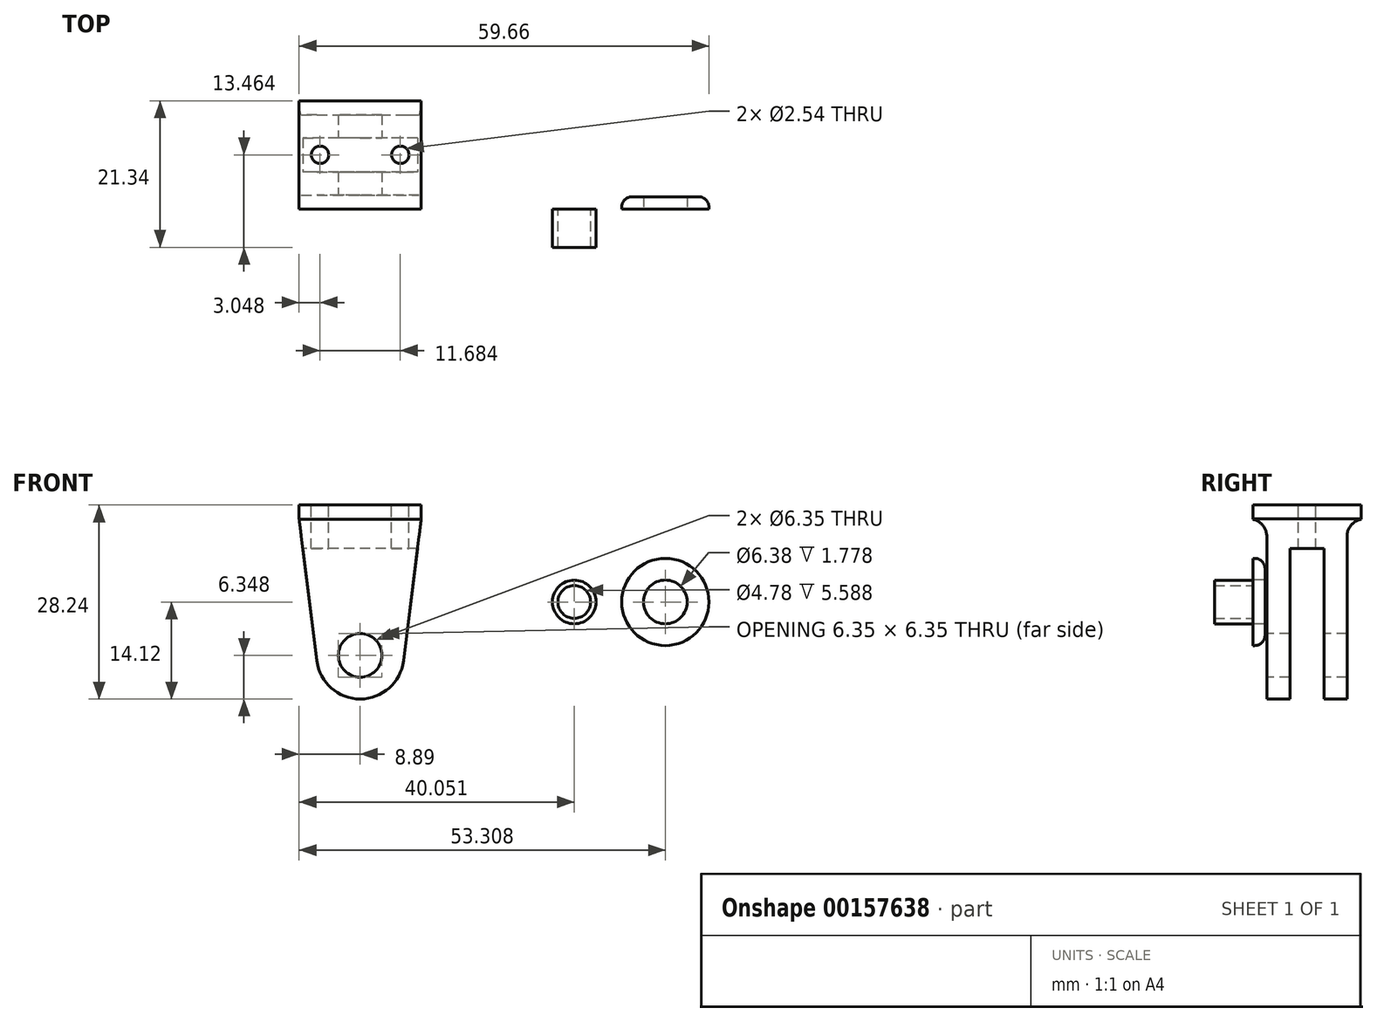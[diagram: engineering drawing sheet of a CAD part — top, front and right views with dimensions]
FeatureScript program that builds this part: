
annotation { "Feature Type Name" : "Feature", "Feature Type Description" : "" }
export const myFeature = defineFeature(function(context is Context, id is Id, definition is map)
    precondition{}
    {
        {
            var Q0;
            Q0=qCreatedBy(makeId("Front.planeOp"),FACE);
            var sketch = newSketch(context, id + "F0", { "sketchPlane" : qUnion([Q0])});
            skLineSegment(sketch, "E0.bottom", {"start": v(8.9, 14.12) * mm, "end": v(-8.89, 14.12) * mm});
            skLineSegment(sketch, "E0.left", {"start": v(8.9, 14.12) * mm, "end": v(8.9, 12.1) * mm});
            skLineSegment(sketch, "E0.right", {"start": v(-8.89, 14.12) * mm, "end": v(-8.89, 12.1) * mm});
            skPoint(sketch, "E0.middle", {"position": v(0, 0) * mm});
            skLineSegment(sketch, "E1", {"start": v(-8.89, 12.1) * mm, "end": v(8.9, 12.1) * mm});
            skArc(sketch, "E2", {"start": v(-6.3, -8.56) * mm, "mid": v(0, -14.12) * mm, "end": v(6.3, -8.56) * mm});
            skLineSegment(sketch, "E3", {"start": v(8.9, 12.1) * mm, "end": v(6.3, -8.56) * mm});
            skLineSegment(sketch, "E4", {"start": v(-8.89, 12.1) * mm, "end": v(-6.3, -8.56) * mm});
            skPoint(sketch, "E5.orphan", {"position": v(8.9, -14.12) * mm});
            skPoint(sketch, "E6.orphan", {"position": v(-8.89, -14.12) * mm});
            skCircle(sketch, "E7", {"center": v(0, -7.77) * mm, "radius": 3.18 * mm});
            skSolve(sketch);
        }
        {
            var Q0;
            Q0=makeQuery(id+"F0.imprint","IMPRINT",FACE,{"disambiguationData":[TD([[makeQuery(id+"F0.imprint","IMPRINT",EDGE,{"derivedFrom":sQuery(id+"F0.wireOp",EDGE,"E0.bottom")}),1.0]])]});
            var Q1;
            Q1=makeQuery(id+"F0.imprint","IMPRINT",FACE,{"disambiguationData":[TD([[makeQuery(id+"F0.imprint","IMPRINT",EDGE,{"derivedFrom":sQuery(id+"F0.wireOp",EDGE,"E1")}),-1.0]])]});
            extrude(context, id + "F1", {"entities" : qUnion([Q0, Q1]), "oppositeDirection" : true, "depth" : 15.75 * mm});
        }
        {
            var Q0;
            Q0=makeQuery(id+"F1.opExtrude","SWEPT_FACE",FACE,{"disambiguationData":[OSD([sQuery(id+"F0.wireOp",EDGE,"E0.right")])]});
            var sketch = newSketch(context, id + "F2", { "sketchPlane" : qUnion([Q0])});
            skLineSegment(sketch, "E8.left", {"start": v(-10.35, 7.77) * mm, "end": v(-10.35, -8.79) * mm});
            skLineSegment(sketch, "E8.right", {"start": v(-5.4, 7.77) * mm, "end": v(-5.4, -8.79) * mm});
            skPoint(sketch, "E8.middle", {"position": v(-7.87, 0) * mm});
            skPoint(sketch, "E8.middle.positionSnap0", {"position": v(-7.87, 12.1) * mm});
            skPoint(sketch, "E8.centerSnap0", {"position": v(-7.87, 12.1) * mm});
            skLineSegment(sketch, "E9", {"start": v(-10.35, -8.79) * mm, "end": v(-10.35, -15.73) * mm});
            skLineSegment(sketch, "E10", {"start": v(-10.35, -15.73) * mm, "end": v(-5.4, -15.73) * mm});
            skLineSegment(sketch, "E11", {"start": v(-5.4, -15.73) * mm, "end": v(-5.4, -8.79) * mm});
            skLineSegment(sketch, "E12", {"start": v(-10.35, 7.77) * mm, "end": v(-5.4, 7.77) * mm});
            skSolve(sketch);
        }
        {
            var Q0;
            Q0=makeQuery(id+"F2.imprint","IMPRINT",FACE,{"disambiguationData":[TD([[makeQuery(id+"F2.imprint","IMPRINT",EDGE,{"derivedFrom":sQuery(id+"F2.wireOp",EDGE,"E8.left")}),1.0]])]});
            extrude(context, id + "F3", {"entities" : qUnion([Q0]), "operationType" : NewBodyOperationType.REMOVE, "endBound" : BoundingType.THROUGH_ALL, "oppositeDirection" : true, "depth" : 25.4 * mm});
        }
        {
            var Q0;
            Q0=makeQuery(id+"F1.opExtrude","SWEPT_FACE",FACE,{"disambiguationData":[OSD([sQuery(id+"F0.wireOp",EDGE,"E0.left")])]});
            var sketch = newSketch(context, id + "F4", { "sketchPlane" : qUnion([Q0])});
            skLineSegment(sketch, "E13", {"start": v(2.03, -59.5) * mm, "end": v(2.03, 9.55) * mm});
            skLineSegment(sketch, "E14", {"start": v(2.03, -59.5) * mm, "end": v(-2.6, -59.5) * mm});
            skLineSegment(sketch, "E15", {"start": v(-2.6, -59.5) * mm, "end": v(-2.6, 12.1) * mm});
            skLineSegment(sketch, "E16", {"start": v(-2.6, 12.1) * mm, "end": v(-0.5, 12.1) * mm});
            skLineSegment(sketch, "E17", {"start": v(13.72, 9.55) * mm, "end": v(13.72, -23.95) * mm});
            skPoint(sketch, "E18.visualSharp", {"position": v(2.03, 12.1) * mm});
            skArc(sketch, "E18.filletArc", {"start": v(2.03, 9.55) * mm, "mid": v(1.29, 11.35) * mm, "end": v(-0.5, 12.1) * mm});
            skLineSegment(sketch, "E19", {"start": v(16.26, 12.1) * mm, "end": v(22.95, 12.1) * mm});
            skLineSegment(sketch, "E20", {"start": v(22.95, 12.1) * mm, "end": v(22.95, -23.95) * mm});
            skLineSegment(sketch, "E21", {"start": v(22.95, -23.95) * mm, "end": v(13.72, -23.95) * mm});
            skPoint(sketch, "E22.visualSharp", {"position": v(13.72, 12.1) * mm});
            skArc(sketch, "E22.filletArc", {"start": v(16.26, 12.1) * mm, "mid": v(14.46, 11.35) * mm, "end": v(13.72, 9.55) * mm});
            skSolve(sketch);
        }
        {
            var Q0;
            Q0=makeQuery(id+"F4.imprint","IMPRINT",FACE,{"disambiguationData":[TD([[makeQuery(id+"F4.imprint","IMPRINT",EDGE,{"derivedFrom":sQuery(id+"F4.wireOp",EDGE,"E17")}),1.0]])]});
            var Q1;
            Q1=makeQuery(id+"F4.imprint","IMPRINT",FACE,{"disambiguationData":[TD([[makeQuery(id+"F4.imprint","IMPRINT",EDGE,{"derivedFrom":sQuery(id+"F4.wireOp",EDGE,"E13")}),1.0]])]});
            extrude(context, id + "F5", {"entities" : qUnion([Q0, Q1]), "operationType" : NewBodyOperationType.REMOVE, "endBound" : BoundingType.THROUGH_ALL, "oppositeDirection" : true, "depth" : 25.4 * mm});
        }
        {
            var Q0;
            Q0=makeQuery(id+"F1.opExtrude","SWEPT_FACE",FACE,{"disambiguationData":[OSD([sQuery(id+"F0.wireOp",EDGE,"E0.bottom")])]});
            var sketch = newSketch(context, id + "F6", { "sketchPlane" : qUnion([Q0])});
            skCircle(sketch, "E23", {"center": v(5.84, 7.87) * mm, "radius": 1.27 * mm});
            skPoint(sketch, "E23.centerSnap0", {"position": v(8.9, 7.87) * mm});
            skCircle(sketch, "E24", {"center": v(-5.84, 7.87) * mm, "radius": 1.27 * mm});
            skSolve(sketch);
        }
        {
            var Q0;
            Q0=makeQuery(id+"F6.imprint","IMPRINT",FACE,{"disambiguationData":[TD([[makeQuery(id+"F6.imprint","IMPRINT",EDGE,{"derivedFrom":sQuery(id+"F6.wireOp",EDGE,"E23")}),1.0]])]});
            var Q1;
            Q1=makeQuery(id+"F6.imprint","IMPRINT",FACE,{"disambiguationData":[TD([[makeQuery(id+"F6.imprint","IMPRINT",EDGE,{"derivedFrom":sQuery(id+"F6.wireOp",EDGE,"E24")}),1.0]])]});
            extrude(context, id + "F7", {"entities" : qUnion([Q0, Q1]), "operationType" : NewBodyOperationType.REMOVE, "oppositeDirection" : true, "depth" : 25.4 * mm});
        }
        {
            var Q0;
            Q0=qCreatedBy(makeId("Front.planeOp"),FACE);
            var sketch = newSketch(context, id + "F8", { "sketchPlane" : qUnion([Q0])});
            skCircle(sketch, "E25", {"center": v(31.16, 0) * mm, "radius": 2.39 * mm});
            skCircle(sketch, "E26", {"center": v(31.16, 0) * mm, "radius": 3.18 * mm});
            skSolve(sketch);
        }
        {
            var Q0;
            Q0=makeQuery(id+"F8.imprint","IMPRINT",FACE,{"disambiguationData":[TD([[makeQuery(id+"F8.imprint","IMPRINT",EDGE,{"derivedFrom":sQuery(id+"F8.wireOp",EDGE,"E25")}),-1.0]])]});
            extrude(context, id + "F9", {"entities" : qUnion([Q0]), "depth" : 5.6 * mm});
        }
        {
            var Q0;
            Q0=qCreatedBy(makeId("Front.planeOp"),FACE);
            var sketch = newSketch(context, id + "F10", { "sketchPlane" : qUnion([Q0])});
            skCircle(sketch, "E27", {"center": v(44.42, 0) * mm, "radius": 3.19 * mm});
            skCircle(sketch, "E28", {"center": v(44.42, 0) * mm, "radius": 6.35 * mm});
            skSolve(sketch);
        }
        {
            var Q0;
            Q0=makeQuery(id+"F10.imprint","IMPRINT",FACE,{"disambiguationData":[TD([[makeQuery(id+"F10.imprint","IMPRINT",EDGE,{"derivedFrom":sQuery(id+"F10.wireOp",EDGE,"E27")}),-1.0]])]});
            extrude(context, id + "F11", {"entities" : qUnion([Q0]), "oppositeDirection" : true, "depth" : 1.78 * mm});
        }
        {
            var Q0;
            Q0=makeQuery(id+"F11.opExtrude","CAP_EDGE",EDGE,{"disambiguationData":[OSD([sQuery(id+"F10.wireOp",EDGE,"E28")])],"isStart":false});
            fillet(context, id + "F12", {"entities" : qUnion([Q0]), "radius" : 1.52 * mm, "tangentPropagation" : true, "allowEdgeOverflow" : false});
        }
    });
